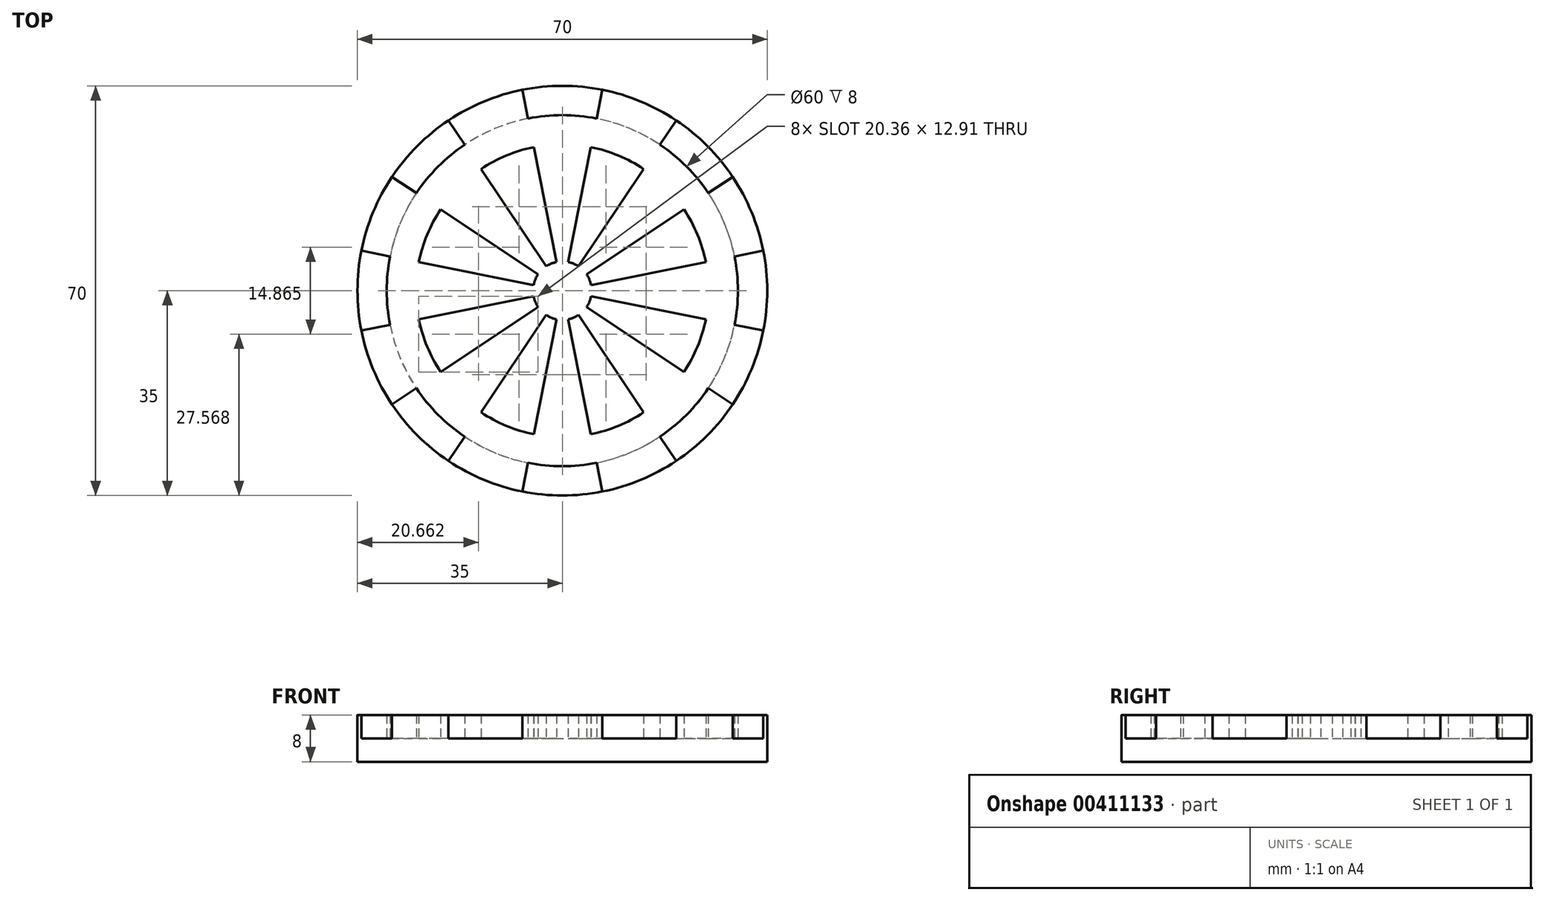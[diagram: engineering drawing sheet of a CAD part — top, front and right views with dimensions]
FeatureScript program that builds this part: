
annotation { "Feature Type Name" : "Feature", "Feature Type Description" : "" }
export const myFeature = defineFeature(function(context is Context, id is Id, definition is map)
    precondition{}
    {
        {
            var Q0;
            Q0=qCreatedBy(makeId("Top.planeOp"),FACE);
            var sketch = newSketch(context, id + "F0", { "sketchPlane" : qUnion([Q0])});
            skCircle(sketch, "E0", {"center": v(0, 0) * mm, "radius": 30 * mm});
            skCircle(sketch, "E1", {"center": v(0, 0) * mm, "radius": 35 * mm});
            skSolve(sketch);
        }
        {
            var Q0;
            Q0=qSketchRegion(id+"F0",true);
            extrude(context, id + "F1", {"entities" : qUnion([Q0]), "depth" : 4 * mm});
        }
        {
            var Q0;
            Q0=makeQuery(id+"F1.opExtrude","CAP_FACE",FACE,{"disambiguationData":[OSD([sQuery(id+"F0.wireOp",EDGE,"E0"),sQuery(id+"F0.wireOp",EDGE,"E1")])],"isStart":false});
            var sketch = newSketch(context, id + "F2", { "sketchPlane" : qUnion([Q0])});
            skPoint(sketch, "E2.0", {"position": v(0, 0) * mm});
            skLineSegment(sketch, "E3", {"start": v(-5.85, 29.42) * mm, "end": v(-6.83, 34.33) * mm});
            skLineSegment(sketch, "E4", {"start": v(5.85, 29.42) * mm, "end": v(6.83, 34.33) * mm});
            skArc(sketch, "E5.0.0", {"start": v(6.83, 34.33) * mm, "mid": v(0, 35) * mm, "end": v(-6.83, 34.33) * mm});
            skArc(sketch, "E6.0", {"start": v(5.85, 29.42) * mm, "mid": v(0, 30) * mm, "end": v(-5.85, 29.42) * mm});
            skLineSegment(sketch, "E7.1.0", {"start": v(-16.67, 24.94) * mm, "end": v(-19.44, 29.1) * mm});
            skLineSegment(sketch, "E7.1.1", {"start": v(-24.94, 16.67) * mm, "end": v(-29.1, 19.44) * mm});
            skArc(sketch, "E7.1.2", {"start": v(-19.44, 29.1) * mm, "mid": v(-24.75, 24.75) * mm, "end": v(-29.1, 19.44) * mm});
            skArc(sketch, "E7.1.3", {"start": v(-16.67, 24.94) * mm, "mid": v(-21.21, 21.21) * mm, "end": v(-24.94, 16.67) * mm});
            skLineSegment(sketch, "E7.2.0", {"start": v(-29.42, 5.85) * mm, "end": v(-34.33, 6.83) * mm});
            skLineSegment(sketch, "E7.2.1", {"start": v(-29.42, -5.85) * mm, "end": v(-34.33, -6.83) * mm});
            skArc(sketch, "E7.2.2", {"start": v(-34.33, 6.83) * mm, "mid": v(-35, 0) * mm, "end": v(-34.33, -6.83) * mm});
            skArc(sketch, "E7.2.3", {"start": v(-29.42, 5.85) * mm, "mid": v(-30, 0) * mm, "end": v(-29.42, -5.85) * mm});
            skLineSegment(sketch, "E7.3.0", {"start": v(-24.94, -16.67) * mm, "end": v(-29.1, -19.44) * mm});
            skLineSegment(sketch, "E7.3.1", {"start": v(-16.67, -24.94) * mm, "end": v(-19.44, -29.1) * mm});
            skArc(sketch, "E7.3.2", {"start": v(-29.1, -19.44) * mm, "mid": v(-24.75, -24.75) * mm, "end": v(-19.44, -29.1) * mm});
            skArc(sketch, "E7.3.3", {"start": v(-24.94, -16.67) * mm, "mid": v(-21.21, -21.21) * mm, "end": v(-16.67, -24.94) * mm});
            skLineSegment(sketch, "E7.4.0", {"start": v(-5.85, -29.42) * mm, "end": v(-6.83, -34.33) * mm});
            skLineSegment(sketch, "E7.4.1", {"start": v(5.85, -29.42) * mm, "end": v(6.83, -34.33) * mm});
            skArc(sketch, "E7.4.2", {"start": v(-6.83, -34.33) * mm, "mid": v(0, -35) * mm, "end": v(6.83, -34.33) * mm});
            skArc(sketch, "E7.4.3", {"start": v(-5.85, -29.42) * mm, "mid": v(0, -30) * mm, "end": v(5.85, -29.42) * mm});
            skLineSegment(sketch, "E7.5.0", {"start": v(16.67, -24.94) * mm, "end": v(19.44, -29.1) * mm});
            skLineSegment(sketch, "E7.5.1", {"start": v(24.94, -16.67) * mm, "end": v(29.1, -19.44) * mm});
            skArc(sketch, "E7.5.2", {"start": v(19.44, -29.1) * mm, "mid": v(24.75, -24.75) * mm, "end": v(29.1, -19.44) * mm});
            skArc(sketch, "E7.5.3", {"start": v(16.67, -24.94) * mm, "mid": v(21.21, -21.21) * mm, "end": v(24.94, -16.67) * mm});
            skLineSegment(sketch, "E7.6.0", {"start": v(29.42, -5.85) * mm, "end": v(34.33, -6.83) * mm});
            skLineSegment(sketch, "E7.6.1", {"start": v(29.42, 5.85) * mm, "end": v(34.33, 6.83) * mm});
            skArc(sketch, "E7.6.2", {"start": v(34.33, -6.83) * mm, "mid": v(35, 0) * mm, "end": v(34.33, 6.83) * mm});
            skArc(sketch, "E7.6.3", {"start": v(29.42, -5.85) * mm, "mid": v(30, 0) * mm, "end": v(29.42, 5.85) * mm});
            skLineSegment(sketch, "E7.7.0", {"start": v(24.94, 16.67) * mm, "end": v(29.1, 19.44) * mm});
            skLineSegment(sketch, "E7.7.1", {"start": v(16.67, 24.94) * mm, "end": v(19.44, 29.1) * mm});
            skArc(sketch, "E7.7.2", {"start": v(29.1, 19.44) * mm, "mid": v(24.75, 24.75) * mm, "end": v(19.44, 29.1) * mm});
            skArc(sketch, "E7.7.3", {"start": v(24.94, 16.67) * mm, "mid": v(21.21, 21.21) * mm, "end": v(16.67, 24.94) * mm});
            skSolve(sketch);
        }
        {
            var Q0;
            Q0=qSketchRegion(id+"F2",true);
            extrude(context, id + "F3", {"entities" : qUnion([Q0]), "operationType" : NewBodyOperationType.ADD, "depth" : 4 * mm});
        }
        {
            var Q0;
            {var subQ0=sQuery(id+"F0.wireOp",EDGE,"E1");var subQ1=sQuery(id+"F0.wireOp",EDGE,"E0");Q0=makeQuery(id+"F3.boolean.opBoolean","SPLIT",FACE,{"disambiguationData":[TD([makeQuery(id+"F3.opExtrude","SWEPT_FACE",FACE,{"disambiguationData":[OSD([sQuery(id+"F2.wireOp",EDGE,"E7.3.1")])]})])],"derivedFrom":makeQuery(id+"F1.opExtrude","CAP_FACE",FACE,{"disambiguationData":[OSD([subQ1,subQ0])],"isStart":false})});}
            var sketch = newSketch(context, id + "F4", { "sketchPlane" : qUnion([Q0])});
            skArc(sketch, "E8.0", {"start": v(-29.1, 19.44) * mm, "mid": v(-32.34, 13.4) * mm, "end": v(-34.33, 6.83) * mm});
            skLineSegment(sketch, "E9.0", {"start": v(-24.94, 16.67) * mm, "end": v(-29.1, 19.44) * mm});
            skLineSegment(sketch, "E10.0", {"start": v(-29.42, 5.85) * mm, "end": v(-34.33, 6.83) * mm});
            skArc(sketch, "E11.0", {"start": v(-29.42, 5.85) * mm, "mid": v(-30, 0) * mm, "end": v(-29.42, -5.85) * mm});
            skLineSegment(sketch, "E12.1.0", {"start": v(-29.42, -5.85) * mm, "end": v(-34.33, -6.83) * mm});
            skArc(sketch, "E12.1.1", {"start": v(-34.33, -6.83) * mm, "mid": v(-32.34, -13.4) * mm, "end": v(-29.1, -19.44) * mm});
            skLineSegment(sketch, "E12.1.2", {"start": v(-24.94, -16.67) * mm, "end": v(-29.1, -19.44) * mm});
            skArc(sketch, "E12.1.3", {"start": v(-24.94, -16.67) * mm, "mid": v(-21.21, -21.21) * mm, "end": v(-16.67, -24.94) * mm});
            skLineSegment(sketch, "E12.2.0", {"start": v(-16.67, -24.94) * mm, "end": v(-19.44, -29.1) * mm});
            skArc(sketch, "E12.2.1", {"start": v(-19.44, -29.1) * mm, "mid": v(-13.4, -32.34) * mm, "end": v(-6.83, -34.33) * mm});
            skLineSegment(sketch, "E12.2.2", {"start": v(-5.85, -29.42) * mm, "end": v(-6.83, -34.33) * mm});
            skArc(sketch, "E12.2.3", {"start": v(-5.85, -29.42) * mm, "mid": v(0, -30) * mm, "end": v(5.85, -29.42) * mm});
            skLineSegment(sketch, "E12.3.0", {"start": v(5.85, -29.42) * mm, "end": v(6.83, -34.33) * mm});
            skArc(sketch, "E12.3.1", {"start": v(6.83, -34.33) * mm, "mid": v(13.4, -32.34) * mm, "end": v(19.44, -29.1) * mm});
            skLineSegment(sketch, "E12.3.2", {"start": v(16.67, -24.94) * mm, "end": v(19.44, -29.1) * mm});
            skArc(sketch, "E12.3.3", {"start": v(16.67, -24.94) * mm, "mid": v(21.21, -21.21) * mm, "end": v(24.94, -16.67) * mm});
            skLineSegment(sketch, "E12.4.0", {"start": v(24.94, -16.67) * mm, "end": v(29.1, -19.44) * mm});
            skArc(sketch, "E12.4.1", {"start": v(29.1, -19.44) * mm, "mid": v(32.34, -13.4) * mm, "end": v(34.33, -6.83) * mm});
            skLineSegment(sketch, "E12.4.2", {"start": v(29.42, -5.85) * mm, "end": v(34.33, -6.83) * mm});
            skArc(sketch, "E12.4.3", {"start": v(29.42, -5.85) * mm, "mid": v(30, 0) * mm, "end": v(29.42, 5.85) * mm});
            skLineSegment(sketch, "E12.5.0", {"start": v(29.42, 5.85) * mm, "end": v(34.33, 6.83) * mm});
            skArc(sketch, "E12.5.1", {"start": v(34.33, 6.83) * mm, "mid": v(32.34, 13.4) * mm, "end": v(29.1, 19.44) * mm});
            skLineSegment(sketch, "E12.5.2", {"start": v(24.94, 16.67) * mm, "end": v(29.1, 19.44) * mm});
            skArc(sketch, "E12.5.3", {"start": v(24.94, 16.67) * mm, "mid": v(21.21, 21.21) * mm, "end": v(16.67, 24.94) * mm});
            skLineSegment(sketch, "E12.6.0", {"start": v(16.67, 24.94) * mm, "end": v(19.44, 29.1) * mm});
            skArc(sketch, "E12.6.1", {"start": v(19.44, 29.1) * mm, "mid": v(13.4, 32.34) * mm, "end": v(6.83, 34.33) * mm});
            skLineSegment(sketch, "E12.6.2", {"start": v(5.85, 29.42) * mm, "end": v(6.83, 34.33) * mm});
            skArc(sketch, "E12.6.3", {"start": v(5.85, 29.42) * mm, "mid": v(0, 30) * mm, "end": v(-5.85, 29.42) * mm});
            skLineSegment(sketch, "E12.7.0", {"start": v(-5.85, 29.42) * mm, "end": v(-6.83, 34.33) * mm});
            skArc(sketch, "E12.7.1", {"start": v(-6.83, 34.33) * mm, "mid": v(-13.4, 32.34) * mm, "end": v(-19.44, 29.1) * mm});
            skLineSegment(sketch, "E12.7.2", {"start": v(-16.67, 24.94) * mm, "end": v(-19.44, 29.1) * mm});
            skArc(sketch, "E12.7.3", {"start": v(-16.67, 24.94) * mm, "mid": v(-21.21, 21.21) * mm, "end": v(-24.94, 16.67) * mm});
            skArc(sketch, "E13", {"start": v(-4.88, 24.52) * mm, "mid": v(-9.57, 23.1) * mm, "end": v(-13.89, 20.79) * mm});
            skLineSegment(sketch, "E14", {"start": v(-0.98, 4.9) * mm, "end": v(-4.88, 24.52) * mm});
            skLineSegment(sketch, "E15.1.0", {"start": v(0.98, 4.9) * mm, "end": v(4.88, 24.52) * mm});
            skLineSegment(sketch, "E15.2.0", {"start": v(2.78, 4.16) * mm, "end": v(13.89, 20.79) * mm});
            skLineSegment(sketch, "E15.3.0", {"start": v(4.16, 2.78) * mm, "end": v(20.79, 13.89) * mm});
            skLineSegment(sketch, "E15.4.0", {"start": v(4.9, 0.98) * mm, "end": v(24.52, 4.88) * mm});
            skLineSegment(sketch, "E15.6.0", {"start": v(4.16, -2.78) * mm, "end": v(20.79, -13.89) * mm});
            skLineSegment(sketch, "E15.7.0", {"start": v(0, 0) * mm, "end": v(13.89, -20.79) * mm});
            skLineSegment(sketch, "E15.8.0", {"start": v(0.98, -4.9) * mm, "end": v(4.88, -24.52) * mm});
            skLineSegment(sketch, "E15.9.0", {"start": v(-0.98, -4.9) * mm, "end": v(-4.88, -24.52) * mm});
            skLineSegment(sketch, "E15.10.0", {"start": v(-2.78, -4.16) * mm, "end": v(-13.89, -20.79) * mm});
            skLineSegment(sketch, "E15.11.0", {"start": v(-4.16, -2.78) * mm, "end": v(-20.79, -13.89) * mm});
            skLineSegment(sketch, "E15.12.0", {"start": v(-4.9, -0.98) * mm, "end": v(-24.52, -4.88) * mm});
            skLineSegment(sketch, "E15.13.0", {"start": v(-4.9, 0.98) * mm, "end": v(-24.52, 4.88) * mm});
            skLineSegment(sketch, "E15.14.0", {"start": v(-4.16, 2.78) * mm, "end": v(-20.79, 13.89) * mm});
            skLineSegment(sketch, "E15.15.0", {"start": v(0, 0) * mm, "end": v(-13.89, 20.79) * mm});
            skLineSegment(sketch, "E15.anchor1", {"start": v(-0.98, 4.9) * mm, "end": v(-4.88, 24.52) * mm, "construction": true});
            skLineSegment(sketch, "E15.anchor2", {"start": v(0, 0) * mm, "end": v(-13.89, 20.79) * mm, "construction": true});
            skArc(sketch, "E16.trimOffspring", {"start": v(13.89, 20.79) * mm, "mid": v(9.57, 23.1) * mm, "end": v(4.88, 24.52) * mm});
            skArc(sketch, "E17.trimOffspring", {"start": v(24.52, 4.88) * mm, "mid": v(23.1, 9.57) * mm, "end": v(20.79, 13.89) * mm});
            skArc(sketch, "E18.trimOffspring", {"start": v(20.79, -13.89) * mm, "mid": v(23.1, -9.57) * mm, "end": v(24.52, -4.88) * mm});
            skArc(sketch, "E19.trimOffspring", {"start": v(4.88, -24.52) * mm, "mid": v(9.57, -23.1) * mm, "end": v(13.89, -20.79) * mm});
            skArc(sketch, "E20.trimOffspring", {"start": v(-13.89, -20.79) * mm, "mid": v(-9.57, -23.1) * mm, "end": v(-4.88, -24.52) * mm});
            skArc(sketch, "E21.trimOffspring", {"start": v(-24.52, -4.88) * mm, "mid": v(-23.1, -9.57) * mm, "end": v(-20.79, -13.89) * mm});
            skArc(sketch, "E22.trimOffspring", {"start": v(-20.79, 13.89) * mm, "mid": v(-23.1, 9.57) * mm, "end": v(-24.52, 4.88) * mm});
            skArc(sketch, "E23", {"start": v(4.9, 0.98) * mm, "mid": v(4.62, 1.91) * mm, "end": v(4.16, 2.78) * mm});
            skLineSegment(sketch, "E24", {"start": v(24.52, -4.88) * mm, "end": v(4.9, -0.98) * mm});
            skArc(sketch, "E25.trimOffspring", {"start": v(4.16, -2.78) * mm, "mid": v(4.62, -1.91) * mm, "end": v(4.9, -0.98) * mm});
            skArc(sketch, "E26.trimOffspring", {"start": v(0.98, -4.9) * mm, "mid": v(1.91, -4.62) * mm, "end": v(2.78, -4.16) * mm});
            skArc(sketch, "E27.trimOffspring", {"start": v(-2.78, -4.16) * mm, "mid": v(-1.91, -4.62) * mm, "end": v(-0.98, -4.9) * mm});
            skArc(sketch, "E28.trimOffspring", {"start": v(-4.9, -0.98) * mm, "mid": v(-4.62, -1.91) * mm, "end": v(-4.16, -2.78) * mm});
            skArc(sketch, "E29.trimOffspring", {"start": v(-4.16, 2.78) * mm, "mid": v(-4.62, 1.91) * mm, "end": v(-4.9, 0.98) * mm});
            skArc(sketch, "E30.trimOffspring", {"start": v(-0.98, 4.9) * mm, "mid": v(-1.91, 4.62) * mm, "end": v(-2.78, 4.16) * mm});
            skArc(sketch, "E31.trimOffspring", {"start": v(2.78, 4.16) * mm, "mid": v(1.91, 4.62) * mm, "end": v(0.98, 4.9) * mm});
            skSolve(sketch);
        }
        {
            var Q0;
            Q0=qSketchRegion(id+"F4",true);
            extrude(context, id + "F5", {"entities" : qUnion([Q0]), "depth" : 4 * mm});
        }
    });
